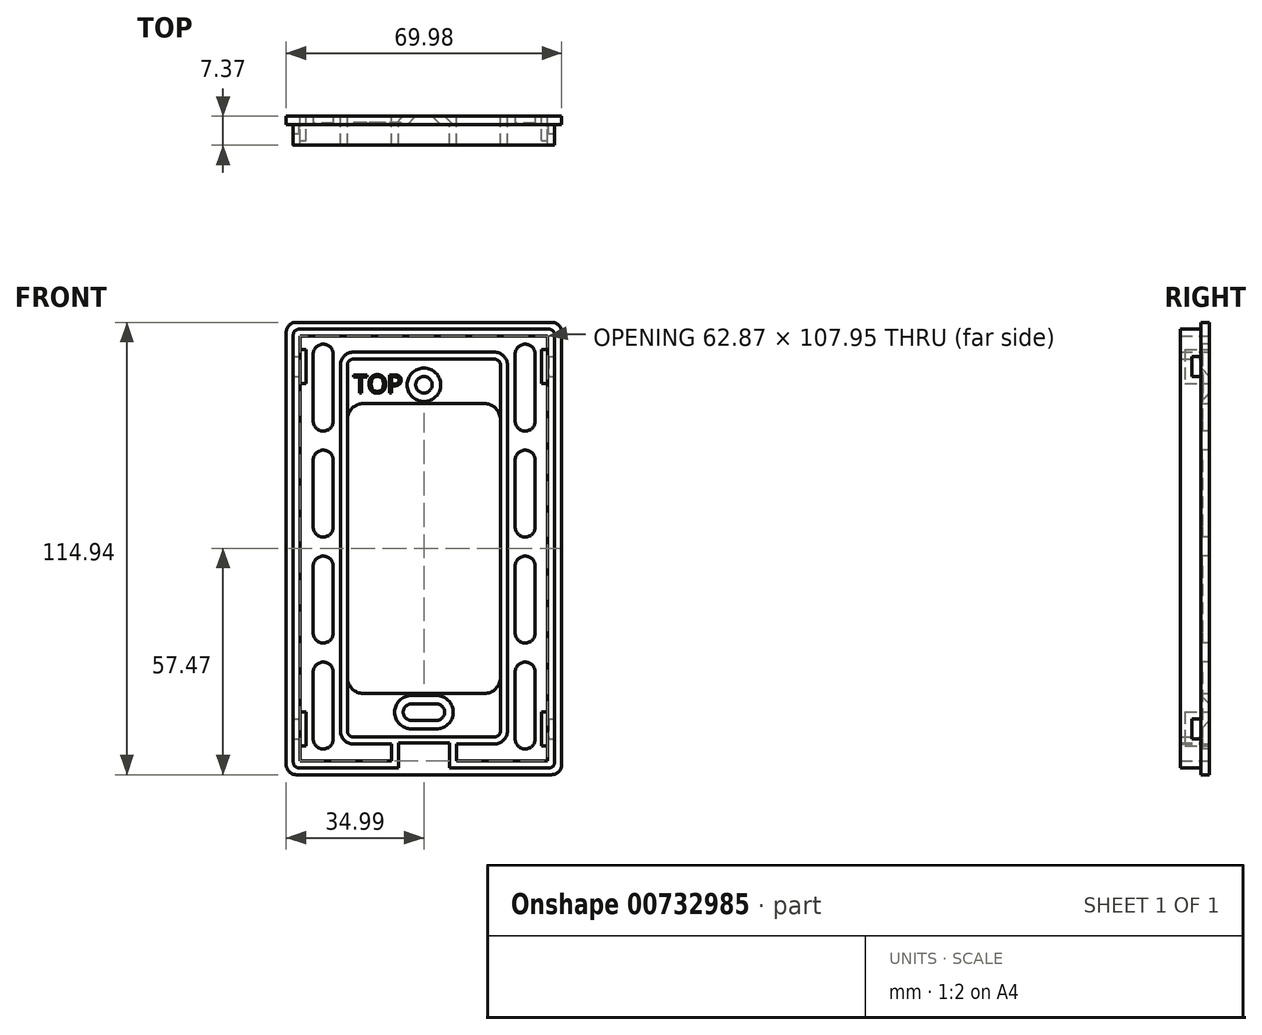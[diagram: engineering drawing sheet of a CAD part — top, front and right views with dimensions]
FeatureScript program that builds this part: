
annotation { "Feature Type Name" : "Feature", "Feature Type Description" : "" }
export const myFeature = defineFeature(function(context is Context, id is Id, definition is map)
    precondition{}
    {
        {
            var Q0;
            Q0=qCreatedBy(makeId("Front.planeOp"),FACE);
            var sketch = newSketch(context, id + "F0", { "sketchPlane" : qUnion([Q0])});
            skLineSegment(sketch, "E0.bottom", {"start": v(32.45, 57.47) * mm, "end": v(-32.45, 57.47) * mm});
            skLineSegment(sketch, "E0.top", {"start": v(32.45, -57.47) * mm, "end": v(-32.45, -57.47) * mm});
            skLineSegment(sketch, "E0.left", {"start": v(34.99, 54.93) * mm, "end": v(34.99, -54.93) * mm});
            skLineSegment(sketch, "E0.right", {"start": v(-34.99, 54.93) * mm, "end": v(-34.99, -54.93) * mm});
            skPoint(sketch, "E0.middle", {"position": v(0, 0) * mm});
            skPoint(sketch, "E1.visualSharp", {"position": v(-34.99, 57.47) * mm});
            skArc(sketch, "E1.filletArc", {"start": v(-32.45, 57.47) * mm, "mid": v(-34.24, 56.72) * mm, "end": v(-34.99, 54.93) * mm});
            skPoint(sketch, "E2.visualSharp", {"position": v(34.99, 57.47) * mm});
            skArc(sketch, "E2.filletArc", {"start": v(34.99, 54.93) * mm, "mid": v(34.24, 56.72) * mm, "end": v(32.45, 57.47) * mm});
            skPoint(sketch, "E3.visualSharp", {"position": v(34.99, -57.47) * mm});
            skArc(sketch, "E3.filletArc", {"start": v(32.45, -57.47) * mm, "mid": v(34.24, -56.72) * mm, "end": v(34.99, -54.93) * mm});
            skPoint(sketch, "E4.visualSharp", {"position": v(-34.99, -57.47) * mm});
            skArc(sketch, "E4.filletArc", {"start": v(-34.99, -54.93) * mm, "mid": v(-34.24, -56.72) * mm, "end": v(-32.45, -57.47) * mm});
            skLineSegment(sketch, "E5.bottom", {"start": v(15.37, 36.83) * mm, "end": v(-15.37, 36.83) * mm});
            skLineSegment(sketch, "E5.top", {"start": v(15.37, -36.83) * mm, "end": v(-15.37, -36.83) * mm});
            skLineSegment(sketch, "E5.left", {"start": v(19.43, 32.77) * mm, "end": v(19.43, -32.77) * mm});
            skLineSegment(sketch, "E5.right", {"start": v(-19.43, 32.77) * mm, "end": v(-19.43, -32.77) * mm});
            skPoint(sketch, "E6.visualSharp", {"position": v(-19.43, 36.83) * mm});
            skArc(sketch, "E6.filletArc", {"start": v(-15.37, 36.83) * mm, "mid": v(-18.24, 35.64) * mm, "end": v(-19.43, 32.77) * mm});
            skPoint(sketch, "E7.visualSharp", {"position": v(19.43, 36.83) * mm});
            skArc(sketch, "E7.filletArc", {"start": v(19.43, 32.77) * mm, "mid": v(18.24, 35.64) * mm, "end": v(15.37, 36.83) * mm});
            skPoint(sketch, "E8.visualSharp", {"position": v(19.43, -36.83) * mm});
            skArc(sketch, "E8.filletArc", {"start": v(15.37, -36.83) * mm, "mid": v(18.24, -35.64) * mm, "end": v(19.43, -32.77) * mm});
            skPoint(sketch, "E9.visualSharp", {"position": v(-19.43, -36.83) * mm});
            skArc(sketch, "E9.filletArc", {"start": v(-19.43, -32.77) * mm, "mid": v(-18.24, -35.64) * mm, "end": v(-15.37, -36.83) * mm});
            skLineSegment(sketch, "E10", {"start": v(0, 41.6) * mm, "end": v(0, -41.6) * mm, "construction": true});
            skCircle(sketch, "E11", {"center": v(0, 41.6) * mm, "radius": 1.97 * mm});
            skLineSegment(sketch, "E12", {"start": v(-34.99, 32.77) * mm, "end": v(-19.43, 32.77) * mm, "construction": true});
            skLineSegment(sketch, "E13", {"start": v(-3.17, -41.6) * mm, "end": v(3.18, -41.6) * mm, "construction": true});
            skArc(sketch, "E14.0.startCap", {"start": v(-3.17, -43.56) * mm, "mid": v(-5.14, -41.6) * mm, "end": v(-3.17, -39.62) * mm});
            skArc(sketch, "E14.0.endCap", {"start": v(3.18, -39.62) * mm, "mid": v(5.14, -41.6) * mm, "end": v(3.18, -43.56) * mm});
            skLineSegment(sketch, "E14.0.left", {"start": v(-3.17, -39.62) * mm, "end": v(3.18, -39.62) * mm});
            skLineSegment(sketch, "E14.0.right", {"start": v(-3.17, -43.56) * mm, "end": v(3.18, -43.56) * mm});
            skSolve(sketch);
        }
        {
            var Q0;
            Q0 = qSketchRegion(id + "F0", true);
            extrude(context, id + "F1", {"entities" : qUnion([Q0]), "depth" : 2.16 * mm, "offsetDistance" : 25.4 * mm});
        }
        {
            var Q0;
            Q0=makeQuery(id+"F1.opExtrude","CAP_FACE",FACE,{"disambiguationData":[OSD([sQuery(id+"F0.wireOp",EDGE,"E0.bottom"),sQuery(id+"F0.wireOp",EDGE,"E0.top"),sQuery(id+"F0.wireOp",EDGE,"E0.left"),sQuery(id+"F0.wireOp",EDGE,"E0.right"),sQuery(id+"F0.wireOp",EDGE,"E1.filletArc"),sQuery(id+"F0.wireOp",EDGE,"E2.filletArc"),sQuery(id+"F0.wireOp",EDGE,"E3.filletArc"),sQuery(id+"F0.wireOp",EDGE,"E4.filletArc"),sQuery(id+"F0.wireOp",EDGE,"E5.bottom"),sQuery(id+"F0.wireOp",EDGE,"E5.top"),sQuery(id+"F0.wireOp",EDGE,"E5.left"),sQuery(id+"F0.wireOp",EDGE,"E5.right"),sQuery(id+"F0.wireOp",EDGE,"E6.filletArc"),sQuery(id+"F0.wireOp",EDGE,"E7.filletArc"),sQuery(id+"F0.wireOp",EDGE,"E8.filletArc"),sQuery(id+"F0.wireOp",EDGE,"E9.filletArc"),sQuery(id+"F0.wireOp",EDGE,"E11"),sQuery(id+"F0.wireOp",EDGE,"euwUtE0h-fWHh-UCWx-4o2V-x830bJ6b2ovp")])],"isStart":false});
            var sketch = newSketch(context, id + "F2", { "sketchPlane" : qUnion([Q0])});
            skCircle(sketch, "E15.0", {"center": v(0, 41.6) * mm, "radius": 1.97 * mm});
            skLineSegment(sketch, "E16.bottom", {"start": v(-31.69, 55.75) * mm, "end": v(31.69, 55.75) * mm});
            skLineSegment(sketch, "E16.top", {"start": v(-31.69, -55.75) * mm, "end": v(-6.48, -55.75) * mm});
            skLineSegment(sketch, "E16.left", {"start": v(-33.21, 54.23) * mm, "end": v(-33.21, 48.77) * mm});
            skLineSegment(sketch, "E16.right", {"start": v(33.21, 54.23) * mm, "end": v(33.21, 48.77) * mm});
            skPoint(sketch, "E16.middle", {"position": v(0, 0) * mm});
            skPoint(sketch, "E17.visualSharp", {"position": v(-33.21, 55.75) * mm});
            skArc(sketch, "E17.filletArc", {"start": v(-31.69, 55.75) * mm, "mid": v(-32.76, 55.3) * mm, "end": v(-33.21, 54.23) * mm});
            skPoint(sketch, "E18.visualSharp", {"position": v(33.21, 55.75) * mm});
            skArc(sketch, "E18.filletArc", {"start": v(33.21, 54.23) * mm, "mid": v(32.76, 55.3) * mm, "end": v(31.69, 55.75) * mm});
            skPoint(sketch, "E19.visualSharp", {"position": v(33.21, -55.75) * mm});
            skArc(sketch, "E19.filletArc", {"start": v(31.69, -55.75) * mm, "mid": v(32.76, -55.3) * mm, "end": v(33.21, -54.23) * mm});
            skPoint(sketch, "E20.visualSharp", {"position": v(-33.21, -55.75) * mm});
            skArc(sketch, "E20.filletArc", {"start": v(-33.21, -54.23) * mm, "mid": v(-32.76, -55.3) * mm, "end": v(-31.69, -55.75) * mm});
            skLineSegment(sketch, "E21.bottom", {"start": v(-17.9, 48.13) * mm, "end": v(17.9, 48.13) * mm});
            skLineSegment(sketch, "E21.top", {"start": v(-17.9, -47.88) * mm, "end": v(17.9, -47.88) * mm});
            skLineSegment(sketch, "E22", {"start": v(-33.21, -48.39) * mm, "end": v(19.37, -48.39) * mm, "construction": true});
            skLineSegment(sketch, "E23.trimOffspring", {"start": v(19.43, 46.6) * mm, "end": v(19.43, -46.36) * mm});
            skLineSegment(sketch, "E24.trimOffspring", {"start": v(-19.43, 46.6) * mm, "end": v(-19.43, -46.36) * mm});
            skLineSegment(sketch, "E25.trimOffspring", {"start": v(-33.21, 48.77) * mm, "end": v(33.21, 48.77) * mm, "construction": true});
            skLineSegment(sketch, "E26.trimOffspring", {"start": v(19.37, -48.39) * mm, "end": v(33.21, -48.39) * mm, "construction": true});
            skLineSegment(sketch, "E27.bottom", {"start": v(31.69, -43.3) * mm, "end": v(33.21, -43.3) * mm});
            skLineSegment(sketch, "E27.top", {"start": v(31.69, -48.39) * mm, "end": v(33.21, -48.39) * mm});
            skLineSegment(sketch, "E27.left", {"start": v(31.69, -43.3) * mm, "end": v(31.69, -48.39) * mm});
            skLineSegment(sketch, "E28.trimOffspring", {"start": v(33.21, -48.39) * mm, "end": v(33.21, -54.23) * mm});
            skLineSegment(sketch, "E29.bottom", {"start": v(31.69, 48.77) * mm, "end": v(33.21, 48.77) * mm});
            skLineSegment(sketch, "E29.top", {"start": v(31.69, 43.69) * mm, "end": v(33.21, 43.69) * mm});
            skLineSegment(sketch, "E29.left", {"start": v(31.69, 48.77) * mm, "end": v(31.69, 43.69) * mm});
            skLineSegment(sketch, "E30.trimOffspring", {"start": v(33.21, 43.69) * mm, "end": v(33.21, -43.3) * mm});
            skLineSegment(sketch, "E31.bottom", {"start": v(-33.21, -43.3) * mm, "end": v(-31.69, -43.3) * mm});
            skLineSegment(sketch, "E31.top", {"start": v(-33.21, -48.39) * mm, "end": v(-31.69, -48.39) * mm});
            skLineSegment(sketch, "E31.right", {"start": v(-31.69, -43.3) * mm, "end": v(-31.69, -48.39) * mm});
            skLineSegment(sketch, "E32.trimOffspring", {"start": v(-33.21, -48.39) * mm, "end": v(-33.21, -54.23) * mm});
            skLineSegment(sketch, "E33.bottom", {"start": v(-33.21, 48.77) * mm, "end": v(-31.69, 48.77) * mm});
            skLineSegment(sketch, "E33.top", {"start": v(-33.21, 43.69) * mm, "end": v(-31.69, 43.69) * mm});
            skLineSegment(sketch, "E33.right", {"start": v(-31.69, 48.77) * mm, "end": v(-31.69, 43.69) * mm});
            skLineSegment(sketch, "E34.trimOffspring", {"start": v(-33.21, 43.69) * mm, "end": v(-33.21, -43.3) * mm});
            skArc(sketch, "E35.filletArc", {"start": v(-17.9, 48.13) * mm, "mid": v(-18.98, 47.69) * mm, "end": v(-19.43, 46.6) * mm});
            skArc(sketch, "E36.filletArc", {"start": v(19.43, 46.6) * mm, "mid": v(18.98, 47.69) * mm, "end": v(17.9, 48.13) * mm});
            skArc(sketch, "E37.filletArc", {"start": v(17.9, -47.88) * mm, "mid": v(18.98, -47.43) * mm, "end": v(19.43, -46.36) * mm});
            skArc(sketch, "E38.filletArc", {"start": v(-19.43, -46.36) * mm, "mid": v(-18.98, -47.43) * mm, "end": v(-17.9, -47.88) * mm});
            skLineSegment(sketch, "E39.top", {"start": v(-6.48, -49.4) * mm, "end": v(6.48, -49.4) * mm});
            skLineSegment(sketch, "E39.left", {"start": v(-6.48, -55.75) * mm, "end": v(-6.48, -49.4) * mm});
            skLineSegment(sketch, "E39.right", {"start": v(6.48, -55.75) * mm, "end": v(6.48, -49.4) * mm});
            skPoint(sketch, "E39.middle", {"position": v(0, -52.58) * mm});
            skLineSegment(sketch, "E40.trimOffspring", {"start": v(6.48, -55.75) * mm, "end": v(31.69, -55.75) * mm});
            skLineSegment(sketch, "E41", {"start": v(-19.43, 41.6) * mm, "end": v(19.43, 41.6) * mm, "construction": true});
            skSolve(sketch);
        }
        {
            var Q0;
            Q0 = qSketchRegion(id + "F2", true);
            extrude(context, id + "F3", {"entities" : qUnion([Q0]), "operationType" : NewBodyOperationType.ADD, "depth" : 2.3 * mm, "offsetDistance" : 25.4 * mm});
        }
        {
            var Q0;
            Q0=makeQuery(id+"F1.opExtrude","CAP_EDGE",EDGE,{"disambiguationData":[OSD([sQuery(id+"F0.wireOp",EDGE,"E11")])],"isStart":false});
            var Q1;
            Q1=makeQuery(id+"F1.opExtrude","CAP_EDGE",EDGE,{"disambiguationData":[OSD([sQuery(id+"F0.wireOp",EDGE,"E14.0.startCap")])],"isStart":false});
            chamfer(context, id + "F4", {"entities" : qUnion([Q0, Q1]), "width" : 2.3 * mm, "tangentPropagation" : true});
        }
        {
            var Q0;
            Q0=makeQuery(id+"F3.opExtrude","CAP_FACE",FACE,{"disambiguationData":[OSD([sQuery(id+"F2.wireOp",EDGE,"E16.bottom"),sQuery(id+"F2.wireOp",EDGE,"E16.top"),sQuery(id+"F2.wireOp",EDGE,"E16.left"),sQuery(id+"F2.wireOp",EDGE,"E16.right"),sQuery(id+"F2.wireOp",EDGE,"E17.filletArc"),sQuery(id+"F2.wireOp",EDGE,"E18.filletArc"),sQuery(id+"F2.wireOp",EDGE,"E19.filletArc"),sQuery(id+"F2.wireOp",EDGE,"E20.filletArc"),sQuery(id+"F2.wireOp",EDGE,"E21.bottom"),sQuery(id+"F2.wireOp",EDGE,"E21.top"),sQuery(id+"F2.wireOp",EDGE,"E23.trimOffspring"),sQuery(id+"F2.wireOp",EDGE,"E24.trimOffspring"),sQuery(id+"F2.wireOp",EDGE,"E27.bottom"),sQuery(id+"F2.wireOp",EDGE,"E27.top"),sQuery(id+"F2.wireOp",EDGE,"E27.left"),sQuery(id+"F2.wireOp",EDGE,"E28.trimOffspring"),sQuery(id+"F2.wireOp",EDGE,"E29.bottom"),sQuery(id+"F2.wireOp",EDGE,"E29.top"),sQuery(id+"F2.wireOp",EDGE,"E29.left"),sQuery(id+"F2.wireOp",EDGE,"E30.trimOffspring"),sQuery(id+"F2.wireOp",EDGE,"E31.bottom"),sQuery(id+"F2.wireOp",EDGE,"E31.top"),sQuery(id+"F2.wireOp",EDGE,"E31.right"),sQuery(id+"F2.wireOp",EDGE,"E32.trimOffspring"),sQuery(id+"F2.wireOp",EDGE,"E33.bottom"),sQuery(id+"F2.wireOp",EDGE,"E33.top"),sQuery(id+"F2.wireOp",EDGE,"E33.right"),sQuery(id+"F2.wireOp",EDGE,"E34.trimOffspring"),sQuery(id+"F2.wireOp",EDGE,"E35.filletArc"),sQuery(id+"F2.wireOp",EDGE,"E36.filletArc"),sQuery(id+"F2.wireOp",EDGE,"E37.filletArc"),sQuery(id+"F2.wireOp",EDGE,"E38.filletArc")])],"isStart":false});
            var sketch = newSketch(context, id + "F5", { "sketchPlane" : qUnion([Q0])});
            skLineSegment(sketch, "E42.0", {"start": v(-19.43, 46.6) * mm, "end": v(-19.43, -46.36) * mm});
            skLineSegment(sketch, "E43.0", {"start": v(19.43, 46.6) * mm, "end": v(19.43, -46.36) * mm});
            skLineSegment(sketch, "E44.0", {"start": v(-17.9, -47.88) * mm, "end": v(17.9, -47.88) * mm});
            skLineSegment(sketch, "E45.0", {"start": v(-17.9, 48.13) * mm, "end": v(17.9, 48.13) * mm});
            skArc(sketch, "E46.0", {"start": v(-17.9, 48.13) * mm, "mid": v(-18.98, 47.69) * mm, "end": v(-19.43, 46.6) * mm});
            skArc(sketch, "E47.0", {"start": v(19.43, 46.6) * mm, "mid": v(18.98, 47.69) * mm, "end": v(17.9, 48.13) * mm});
            skArc(sketch, "E48.0", {"start": v(-19.43, -46.36) * mm, "mid": v(-18.98, -47.43) * mm, "end": v(-17.9, -47.88) * mm});
            skArc(sketch, "E48.1", {"start": v(17.9, -47.88) * mm, "mid": v(18.98, -47.43) * mm, "end": v(19.43, -46.36) * mm});
            skArc(sketch, "E48.2", {"start": v(-33.21, -54.23) * mm, "mid": v(-32.76, -55.3) * mm, "end": v(-31.69, -55.75) * mm});
            skLineSegment(sketch, "E48.3", {"start": v(-31.69, -55.75) * mm, "end": v(-31.69, -55.75) * mm});
            skArc(sketch, "E48.4", {"start": v(31.69, -55.75) * mm, "mid": v(32.76, -55.3) * mm, "end": v(33.21, -54.23) * mm});
            skArc(sketch, "E49.0", {"start": v(33.21, 54.23) * mm, "mid": v(32.76, 55.3) * mm, "end": v(31.69, 55.75) * mm});
            skLineSegment(sketch, "E49.1", {"start": v(-31.69, 55.75) * mm, "end": v(31.69, 55.75) * mm});
            skArc(sketch, "E49.2", {"start": v(-31.69, 55.75) * mm, "mid": v(-32.76, 55.3) * mm, "end": v(-33.21, 54.23) * mm});
            skLineSegment(sketch, "E50", {"start": v(-33.21, 54.23) * mm, "end": v(-33.21, -54.23) * mm});
            skLineSegment(sketch, "E51", {"start": v(33.21, 54.23) * mm, "end": v(33.21, -54.23) * mm});
            skLineSegment(sketch, "E52", {"start": v(-31.69, -55.75) * mm, "end": v(-6.48, -55.75) * mm});
            skLineSegment(sketch, "E53.0", {"start": v(-6.48, -55.75) * mm, "end": v(-6.48, -49.4) * mm});
            skLineSegment(sketch, "E54.0", {"start": v(-6.48, -49.4) * mm, "end": v(6.48, -49.4) * mm});
            skLineSegment(sketch, "E55.0", {"start": v(6.48, -55.75) * mm, "end": v(6.48, -49.4) * mm});
            skLineSegment(sketch, "E56.trimOffspring", {"start": v(6.48, -55.75) * mm, "end": v(31.69, -55.75) * mm});
            skSolve(sketch);
        }
        {
            var Q0;
            Q0 = qSketchRegion(id + "F5", true);
            extrude(context, id + "F6", {"entities" : qUnion([Q0]), "operationType" : NewBodyOperationType.ADD, "depth" : 2.92 * mm, "offsetDistance" : 25.4 * mm});
        }
        {
            var Q0;
            Q0=makeQuery(id+"F6.opExtrude","CAP_FACE",FACE,{"disambiguationData":[OSD([sQuery(id+"F5.wireOp",EDGE,"E42.0"),sQuery(id+"F5.wireOp",EDGE,"E43.0"),sQuery(id+"F5.wireOp",EDGE,"E44.0"),sQuery(id+"F5.wireOp",EDGE,"E45.0"),sQuery(id+"F5.wireOp",EDGE,"E46.0"),sQuery(id+"F5.wireOp",EDGE,"E47.0"),sQuery(id+"F5.wireOp",EDGE,"E48.0"),sQuery(id+"F5.wireOp",EDGE,"E48.1"),sQuery(id+"F5.wireOp",EDGE,"E48.2"),sQuery(id+"F5.wireOp",EDGE,"E48.4"),sQuery(id+"F5.wireOp",EDGE,"E49.0"),sQuery(id+"F5.wireOp",EDGE,"E49.1"),sQuery(id+"F5.wireOp",EDGE,"E49.2"),sQuery(id+"F5.wireOp",EDGE,"E50"),sQuery(id+"F5.wireOp",EDGE,"E51"),sQuery(id+"F5.wireOp",EDGE,"E52")])],"isStart":false});
            shell(context, id + "F7", {"entities" : qUnion([Q0]), "thickness" : 1.78 * mm});
        }
        {
            var Q0;
            {var subQ0=sQuery(id+"F0.wireOp",EDGE,"E6.filletArc");var subQ1=sQuery(id+"F0.wireOp",EDGE,"E11");var subQ2=sQuery(id+"F0.wireOp",EDGE,"E7.filletArc");var subQ3=sQuery(id+"F0.wireOp",EDGE,"E5.bottom");var subQ4=sQuery(id+"F0.wireOp",EDGE,"E5.left");var subQ5=sQuery(id+"F0.wireOp",EDGE,"E5.right");Q0=makeQuery(id+"F3.boolean.opBoolean","SPLIT",FACE,{"disambiguationData":[TD([makeQuery(id+"F1.opExtrude","SWEPT_FACE",FACE,{"disambiguationData":[OSD([subQ3])]})])],"derivedFrom":makeQuery(id+"F1.opExtrude","CAP_FACE",FACE,{"disambiguationData":[OSD([sQuery(id+"F0.wireOp",EDGE,"E0.bottom"),sQuery(id+"F0.wireOp",EDGE,"E0.top"),sQuery(id+"F0.wireOp",EDGE,"E0.left"),sQuery(id+"F0.wireOp",EDGE,"E0.right"),sQuery(id+"F0.wireOp",EDGE,"E1.filletArc"),sQuery(id+"F0.wireOp",EDGE,"E2.filletArc"),sQuery(id+"F0.wireOp",EDGE,"E3.filletArc"),sQuery(id+"F0.wireOp",EDGE,"E4.filletArc"),subQ3,sQuery(id+"F0.wireOp",EDGE,"E5.top"),subQ4,subQ5,subQ0,subQ2,sQuery(id+"F0.wireOp",EDGE,"E8.filletArc"),sQuery(id+"F0.wireOp",EDGE,"E9.filletArc"),subQ1,sQuery(id+"F0.wireOp",EDGE,"euwUtE0h-fWHh-UCWx-4o2V-x830bJ6b2ovp")])],"isStart":false})});}
            var sketch = newSketch(context, id + "F8", { "sketchPlane" : qUnion([Q0])});
            skText(sketch, "E57", { "text": "TOP\n", "fontName": "OpenSans-Regular.ttf"});
            const initialGuessF8  = {"E57": [-0.0179, 0.03952, 1, 0, 0.00463]};
            skSetInitialGuess(sketch, initialGuessF8);
            skSolve(sketch);
        }
        {
            var Q0;
            Q0 = qSketchRegion(id + "F8", true);
            extrude(context, id + "F9", {"entities" : qUnion([Q0]), "operationType" : NewBodyOperationType.REMOVE, "oppositeDirection" : true, "depth" : 0.5 * mm, "offsetDistance" : 25.4 * mm});
        }
        {
            var Q0;
            Q0=makeQuery(id+"F7.opShell","OFFSET_FACE",FACE,{"disambiguationData":[OSD([sQuery(id+"F0.wireOp",EDGE,"E0.bottom"),sQuery(id+"F0.wireOp",EDGE,"E0.top"),sQuery(id+"F0.wireOp",EDGE,"E0.left"),sQuery(id+"F0.wireOp",EDGE,"E0.right"),sQuery(id+"F0.wireOp",EDGE,"E1.filletArc"),sQuery(id+"F0.wireOp",EDGE,"E2.filletArc"),sQuery(id+"F0.wireOp",EDGE,"E3.filletArc"),sQuery(id+"F0.wireOp",EDGE,"E4.filletArc"),sQuery(id+"F0.wireOp",EDGE,"E5.bottom"),sQuery(id+"F0.wireOp",EDGE,"E5.top"),sQuery(id+"F0.wireOp",EDGE,"E5.left"),sQuery(id+"F0.wireOp",EDGE,"E5.right"),sQuery(id+"F0.wireOp",EDGE,"E6.filletArc"),sQuery(id+"F0.wireOp",EDGE,"E7.filletArc"),sQuery(id+"F0.wireOp",EDGE,"E8.filletArc"),sQuery(id+"F0.wireOp",EDGE,"E9.filletArc"),sQuery(id+"F0.wireOp",EDGE,"E11"),sQuery(id+"F0.wireOp",EDGE,"euwUtE0h-fWHh-UCWx-4o2V-x830bJ6b2ovp")])]});
            var sketch = newSketch(context, id + "F10", { "sketchPlane" : qUnion([Q0])});
            skLineSegment(sketch, "E58", {"start": v(-25.57, 49.4) * mm, "end": v(-25.57, 32.4) * mm});
            skArc(sketch, "E59.0.startCap", {"start": v(-28.11, 49.4) * mm, "mid": v(-25.57, 51.93) * mm, "end": v(-23.03, 49.4) * mm});
            skArc(sketch, "E59.0.endCap", {"start": v(-23.03, 32.4) * mm, "mid": v(-25.57, 29.86) * mm, "end": v(-28.11, 32.4) * mm});
            skLineSegment(sketch, "E59.0.left", {"start": v(-23.03, 49.4) * mm, "end": v(-23.03, 32.4) * mm});
            skLineSegment(sketch, "E59.0.right", {"start": v(-28.11, 49.4) * mm, "end": v(-28.11, 32.4) * mm});
            skArc(sketch, "E60.0.1.0", {"start": v(-28.11, 22.47) * mm, "mid": v(-25.57, 25) * mm, "end": v(-23.03, 22.47) * mm});
            skLineSegment(sketch, "E60.0.1.1", {"start": v(-23.03, 22.47) * mm, "end": v(-23.03, 5.47) * mm});
            skArc(sketch, "E60.0.1.2", {"start": v(-23.03, 5.47) * mm, "mid": v(-25.57, 2.93) * mm, "end": v(-28.11, 5.47) * mm});
            skLineSegment(sketch, "E60.0.1.3", {"start": v(-28.11, 22.47) * mm, "end": v(-28.11, 5.47) * mm});
            skArc(sketch, "E60.0.2.0", {"start": v(-28.11, -4.45) * mm, "mid": v(-25.57, -1.91) * mm, "end": v(-23.03, -4.45) * mm});
            skLineSegment(sketch, "E60.0.2.1", {"start": v(-23.03, -4.45) * mm, "end": v(-23.03, -21.45) * mm});
            skArc(sketch, "E60.0.2.2", {"start": v(-23.03, -21.45) * mm, "mid": v(-25.57, -24) * mm, "end": v(-28.11, -21.45) * mm});
            skLineSegment(sketch, "E60.0.2.3", {"start": v(-28.11, -4.45) * mm, "end": v(-28.11, -21.45) * mm});
            skArc(sketch, "E60.0.3.0", {"start": v(-28.11, -31.38) * mm, "mid": v(-25.57, -28.84) * mm, "end": v(-23.03, -31.38) * mm});
            skLineSegment(sketch, "E60.0.3.1", {"start": v(-23.03, -31.38) * mm, "end": v(-23.03, -48.38) * mm});
            skArc(sketch, "E60.0.3.2", {"start": v(-23.03, -48.38) * mm, "mid": v(-25.57, -50.92) * mm, "end": v(-28.11, -48.38) * mm});
            skLineSegment(sketch, "E60.0.3.3", {"start": v(-28.11, -31.38) * mm, "end": v(-28.11, -48.38) * mm});
            skArc(sketch, "E60.1.0.0", {"start": v(23.2, 49.4) * mm, "mid": v(25.73, 51.93) * mm, "end": v(28.27, 49.4) * mm});
            skLineSegment(sketch, "E60.1.0.1", {"start": v(28.27, 49.4) * mm, "end": v(28.27, 32.4) * mm});
            skArc(sketch, "E60.1.0.2", {"start": v(28.27, 32.4) * mm, "mid": v(25.73, 29.86) * mm, "end": v(23.2, 32.4) * mm});
            skLineSegment(sketch, "E60.1.0.3", {"start": v(23.2, 49.4) * mm, "end": v(23.2, 32.4) * mm});
            skArc(sketch, "E60.1.1.0", {"start": v(23.2, 22.47) * mm, "mid": v(25.73, 25) * mm, "end": v(28.27, 22.47) * mm});
            skLineSegment(sketch, "E60.1.1.1", {"start": v(28.27, 22.47) * mm, "end": v(28.27, 5.47) * mm});
            skArc(sketch, "E60.1.1.2", {"start": v(28.27, 5.47) * mm, "mid": v(25.73, 2.93) * mm, "end": v(23.2, 5.47) * mm});
            skLineSegment(sketch, "E60.1.1.3", {"start": v(23.2, 22.47) * mm, "end": v(23.2, 5.47) * mm});
            skArc(sketch, "E60.1.2.0", {"start": v(23.2, -4.45) * mm, "mid": v(25.73, -1.91) * mm, "end": v(28.27, -4.45) * mm});
            skLineSegment(sketch, "E60.1.2.1", {"start": v(28.27, -4.45) * mm, "end": v(28.27, -21.45) * mm});
            skArc(sketch, "E60.1.2.2", {"start": v(28.27, -21.45) * mm, "mid": v(25.73, -24) * mm, "end": v(23.2, -21.45) * mm});
            skLineSegment(sketch, "E60.1.2.3", {"start": v(23.2, -4.45) * mm, "end": v(23.2, -21.45) * mm});
            skArc(sketch, "E60.1.3.0", {"start": v(23.2, -31.38) * mm, "mid": v(25.73, -28.84) * mm, "end": v(28.27, -31.38) * mm});
            skLineSegment(sketch, "E60.1.3.1", {"start": v(28.27, -31.38) * mm, "end": v(28.27, -48.38) * mm});
            skArc(sketch, "E60.1.3.2", {"start": v(28.27, -48.38) * mm, "mid": v(25.73, -50.92) * mm, "end": v(23.2, -48.38) * mm});
            skLineSegment(sketch, "E60.1.3.3", {"start": v(23.2, -31.38) * mm, "end": v(23.2, -48.38) * mm});
            skLineSegment(sketch, "E60.direction1", {"start": v(-28.11, 32.4) * mm, "end": v(23.2, 32.4) * mm, "construction": true});
            skLineSegment(sketch, "E60.direction2", {"start": v(-28.11, 32.4) * mm, "end": v(-28.11, 5.47) * mm, "construction": true});
            skSolve(sketch);
        }
        {
            var Q0;
            Q0=makeQuery(id+"F10.imprint","IMPRINT",FACE,{"disambiguationData":[TD([[makeQuery(id+"F10.imprint","IMPRINT",EDGE,{"derivedFrom":sQuery(id+"F10.wireOp",EDGE,"E59.0.startCap")}),-1.0]])]});
            var Q1;
            Q1=makeQuery(id+"F10.imprint","IMPRINT",FACE,{"disambiguationData":[TD([[makeQuery(id+"F10.imprint","IMPRINT",EDGE,{"derivedFrom":sQuery(id+"F10.wireOp",EDGE,"E60.0.1.0")}),-1.0]])]});
            var Q2;
            Q2=makeQuery(id+"F10.imprint","IMPRINT",FACE,{"disambiguationData":[TD([[makeQuery(id+"F10.imprint","IMPRINT",EDGE,{"derivedFrom":sQuery(id+"F10.wireOp",EDGE,"E60.0.2.0")}),-1.0]])]});
            var Q3;
            Q3=makeQuery(id+"F10.imprint","IMPRINT",FACE,{"disambiguationData":[TD([[makeQuery(id+"F10.imprint","IMPRINT",EDGE,{"derivedFrom":sQuery(id+"F10.wireOp",EDGE,"E60.0.3.0")}),-1.0]])]});
            var Q4;
            Q4=makeQuery(id+"F10.imprint","IMPRINT",FACE,{"disambiguationData":[TD([[makeQuery(id+"F10.imprint","IMPRINT",EDGE,{"derivedFrom":sQuery(id+"F10.wireOp",EDGE,"E60.1.3.0")}),-1.0]])]});
            var Q5;
            Q5=makeQuery(id+"F10.imprint","IMPRINT",FACE,{"disambiguationData":[TD([[makeQuery(id+"F10.imprint","IMPRINT",EDGE,{"derivedFrom":sQuery(id+"F10.wireOp",EDGE,"E60.1.2.0")}),-1.0]])]});
            var Q6;
            Q6=makeQuery(id+"F10.imprint","IMPRINT",FACE,{"disambiguationData":[TD([[makeQuery(id+"F10.imprint","IMPRINT",EDGE,{"derivedFrom":sQuery(id+"F10.wireOp",EDGE,"E60.1.1.0")}),-1.0]])]});
            var Q7;
            Q7=makeQuery(id+"F10.imprint","IMPRINT",FACE,{"disambiguationData":[TD([[makeQuery(id+"F10.imprint","IMPRINT",EDGE,{"derivedFrom":sQuery(id+"F10.wireOp",EDGE,"E60.1.0.0")}),-1.0]])]});
            extrude(context, id + "F11", {"entities" : qUnion([Q0, Q1, Q2, Q3, Q4, Q5, Q6, Q7]), "operationType" : NewBodyOperationType.REMOVE, "endBound" : BoundingType.THROUGH_ALL, "oppositeDirection" : true, "depth" : 25.4 * mm, "offsetDistance" : 25.4 * mm});
        }
    });
